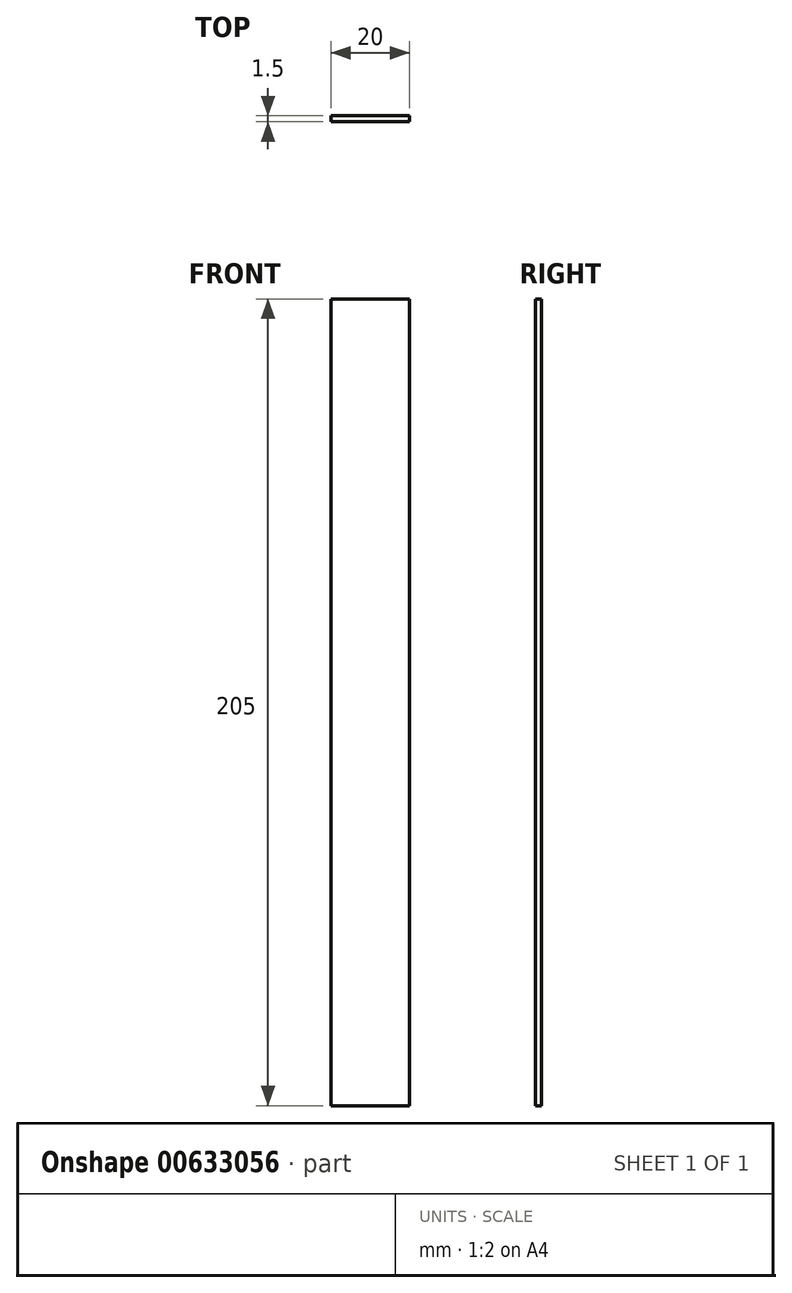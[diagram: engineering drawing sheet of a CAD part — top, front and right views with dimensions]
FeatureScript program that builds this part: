
annotation { "Feature Type Name" : "Feature", "Feature Type Description" : "" }
export const myFeature = defineFeature(function(context is Context, id is Id, definition is map)
    precondition{}
    {
        {
            var Q0;
            Q0=qCreatedBy(makeId("Front.planeOp"),FACE);
            var sketch = newSketch(context, id + "F0", { "sketchPlane" : qUnion([Q0])});
            skLineSegment(sketch, "E0.bottom", {"start": v(0, 0) * mm, "end": v(20, 0) * mm});
            skLineSegment(sketch, "E0.top", {"start": v(0, -205) * mm, "end": v(20, -205) * mm});
            skLineSegment(sketch, "E0.left", {"start": v(0, 0) * mm, "end": v(0, -205) * mm});
            skLineSegment(sketch, "E0.right", {"start": v(20, 0) * mm, "end": v(20, -205) * mm});
            skSolve(sketch);
        }
        {
            var Q0;
            Q0=makeQuery(id+"F0.imprint","IMPRINT",FACE,{"disambiguationData":[TD([[makeQuery(id+"F0.imprint","IMPRINT",EDGE,{"derivedFrom":sQuery(id+"F0.wireOp",EDGE,"E0.bottom")}),-1.0]])]});
            extrude(context, id + "F1", {"entities" : qUnion([Q0]), "depth" : 1.5 * mm, "offsetDistance" : 25 * mm});
        }
    });
